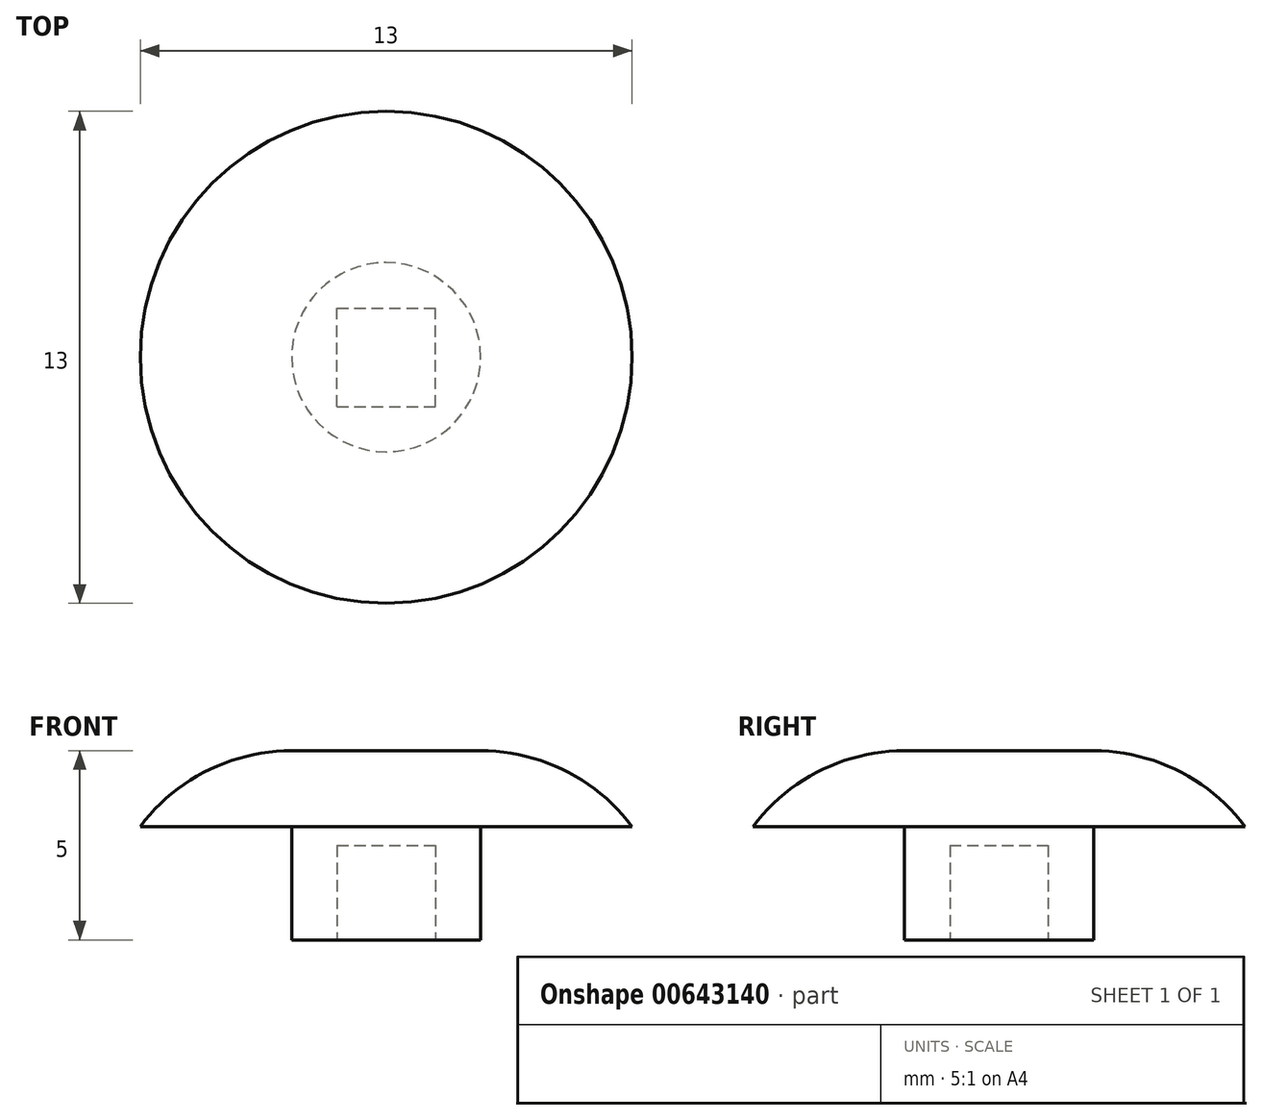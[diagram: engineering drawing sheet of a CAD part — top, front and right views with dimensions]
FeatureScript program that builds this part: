
annotation { "Feature Type Name" : "Feature", "Feature Type Description" : "" }
export const myFeature = defineFeature(function(context is Context, id is Id, definition is map)
    precondition{}
    {
        {
            var Q0;
            Q0=qCreatedBy(makeId("Top.planeOp"),FACE);
            var sketch = newSketch(context, id + "F0", { "sketchPlane" : qUnion([Q0])});
            skCircle(sketch, "E0", {"center": v(0, 0) * mm, "radius": 7.5 * mm});
            skSolve(sketch);
        }
        {
            var Q0;
            Q0 = qSketchRegion(id + "F0", true);
            extrude(context, id + "F1", {"entities" : qUnion([Q0]), "depth" : 5 * mm, "offsetDistance" : 25 * mm});
        }
        {
            var Q0;
            Q0=makeQuery(id+"F1.opExtrude","CAP_EDGE",EDGE,{"disambiguationData":[OSD([sQuery(id+"F0.wireOp",EDGE,"E0")])],"isStart":false});
            fillet(context, id + "F2", {"entities" : qUnion([Q0]), "radius" : 5 * mm, "tangentPropagation" : true, "allowEdgeOverflow" : false});
        }
        {
            var Q0;
            Q0=makeQuery(id+"F1.opExtrude","CAP_FACE",FACE,{"disambiguationData":[OSD([sQuery(id+"F0.wireOp",EDGE,"E0")])],"isStart":true});
            var sketch = newSketch(context, id + "F3", { "sketchPlane" : qUnion([Q0])});
            skLineSegment(sketch, "E1.bottom", {"start": v(-1.3, 1.3) * mm, "end": v(1.3, 1.3) * mm});
            skLineSegment(sketch, "E1.top", {"start": v(-1.3, -1.3) * mm, "end": v(1.3, -1.3) * mm});
            skLineSegment(sketch, "E1.left", {"start": v(-1.3, 1.3) * mm, "end": v(-1.3, -1.3) * mm});
            skLineSegment(sketch, "E1.right", {"start": v(1.3, 1.3) * mm, "end": v(1.3, -1.3) * mm});
            skSolve(sketch);
        }
        {
            var Q0;
            Q0 = qSketchRegion(id + "F3", true);
            extrude(context, id + "F4", {"entities" : qUnion([Q0]), "operationType" : NewBodyOperationType.REMOVE, "oppositeDirection" : true, "depth" : 2.5 * mm, "offsetDistance" : 25 * mm});
        }
        {
            var Q0;
            Q0=makeQuery(id+"F1.opExtrude","CAP_FACE",FACE,{"disambiguationData":[OSD([sQuery(id+"F0.wireOp",EDGE,"E0")])],"isStart":true});
            var sketch = newSketch(context, id + "F5", { "sketchPlane" : qUnion([Q0])});
            skCircle(sketch, "E2", {"center": v(0, 0) * mm, "radius": 2.5 * mm});
            skCircle(sketch, "E3", {"center": v(0, 0) * mm, "radius": 7.5 * mm});
            skSolve(sketch);
        }
        {
            var Q0;
            Q0=makeQuery(id+"F5.imprint","IMPRINT",FACE,{"disambiguationData":[TD([[makeQuery(id+"F5.imprint","IMPRINT",EDGE,{"derivedFrom":sQuery(id+"F5.wireOp",EDGE,"E2")}),-1.0]])]});
            extrude(context, id + "F6", {"entities" : qUnion([Q0]), "operationType" : NewBodyOperationType.REMOVE, "oppositeDirection" : true, "depth" : 3 * mm, "offsetDistance" : 25 * mm});
        }
    });
